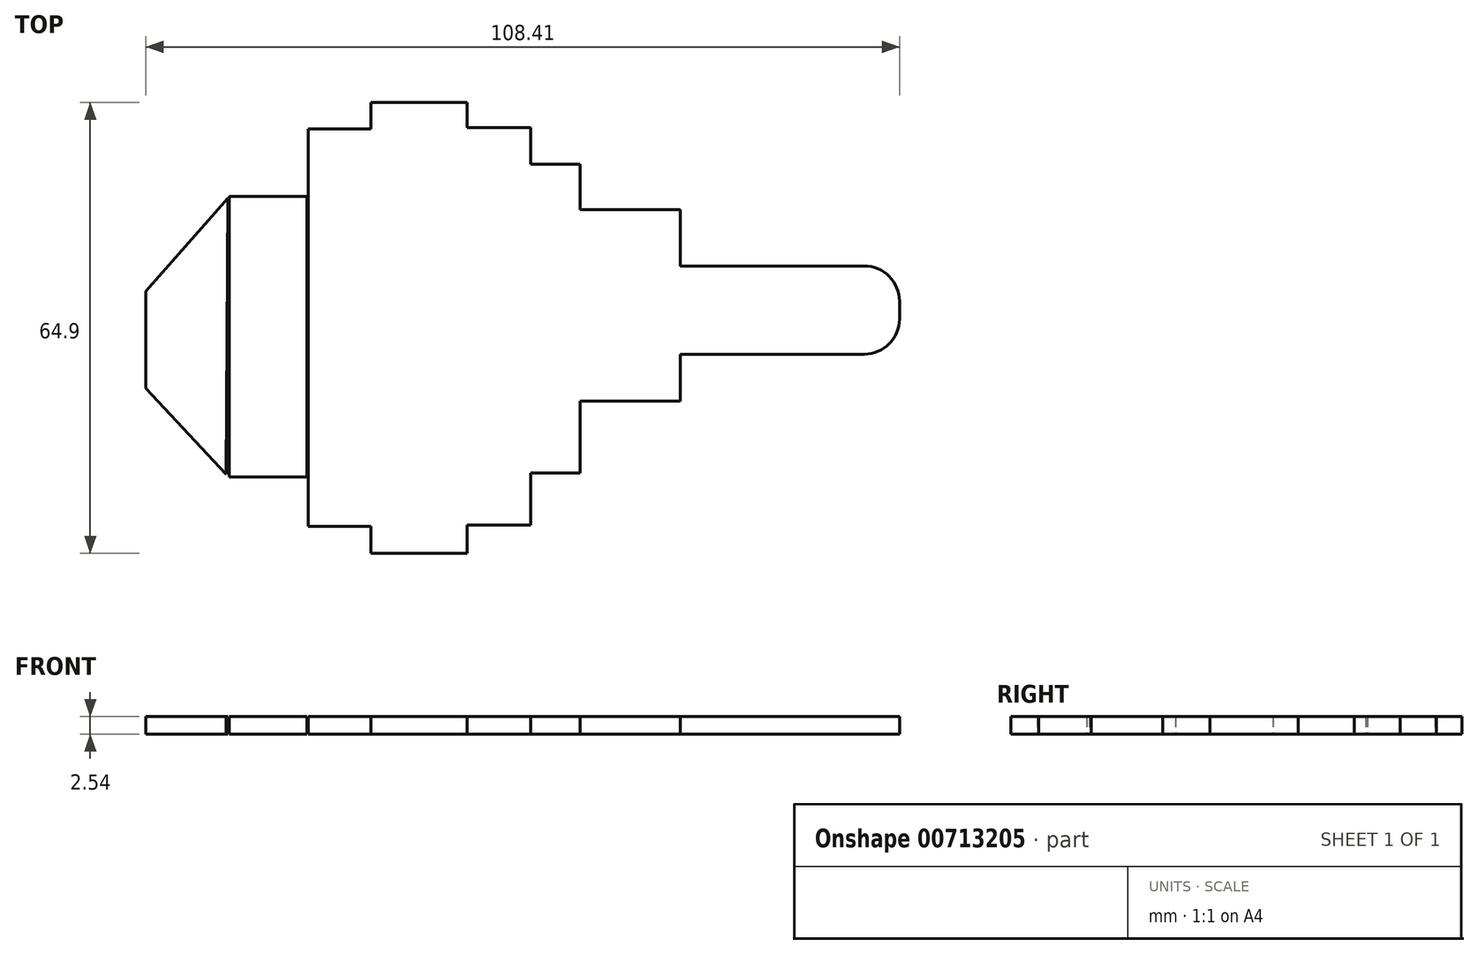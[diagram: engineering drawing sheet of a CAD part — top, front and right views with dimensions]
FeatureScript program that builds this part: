
annotation { "Feature Type Name" : "Feature", "Feature Type Description" : "" }
export const myFeature = defineFeature(function(context is Context, id is Id, definition is map)
    precondition{}
    {
        {
            var Q0;
            Q0=qCreatedBy(makeId("Top.planeOp"),FACE);
            var sketch = newSketch(context, id + "F0", { "sketchPlane" : qUnion([Q0])});
            skLineSegment(sketch, "E0.bottom", {"start": v(44.31, 7.48) * mm, "end": v(70.98, 7.48) * mm});
            skLineSegment(sketch, "E0.top", {"start": v(44.31, -5.22) * mm, "end": v(70.98, -5.22) * mm});
            skLineSegment(sketch, "E0.left", {"start": v(44.31, 7.48) * mm, "end": v(44.31, -5.22) * mm});
            skLineSegment(sketch, "E0.right", {"start": v(76.06, 2.4) * mm, "end": v(76.06, -0.14) * mm});
            skPoint(sketch, "E1.visualSharp", {"position": v(76.06, 7.48) * mm});
            skArc(sketch, "E1.filletArc", {"start": v(76.06, 2.4) * mm, "mid": v(74.58, 6) * mm, "end": v(70.98, 7.48) * mm});
            skPoint(sketch, "E2.visualSharp", {"position": v(76.06, -5.22) * mm});
            skArc(sketch, "E2.filletArc", {"start": v(70.98, -5.22) * mm, "mid": v(74.58, -3.73) * mm, "end": v(76.06, -0.14) * mm});
            skSolve(sketch);
        }
        {
            var Q0;
            Q0 = qSketchRegion(id + "F0", true);
            extrude(context, id + "F1", {"entities" : qUnion([Q0]), "depth" : 2.54 * mm, "offsetDistance" : 25.4 * mm});
        }
        {
            var Q0;
            Q0=qCreatedBy(makeId("Top.planeOp"),FACE);
            var sketch = newSketch(context, id + "F2", { "sketchPlane" : qUnion([Q0])});
            skLineSegment(sketch, "E3.bottom", {"start": v(44.52, -11.97) * mm, "end": v(29.92, -11.97) * mm});
            skLineSegment(sketch, "E3.top", {"start": v(44.52, 15.6) * mm, "end": v(29.92, 15.6) * mm});
            skLineSegment(sketch, "E3.left", {"start": v(44.52, -11.97) * mm, "end": v(44.52, 15.6) * mm});
            skLineSegment(sketch, "E3.right", {"start": v(29.92, -11.97) * mm, "end": v(29.92, 15.6) * mm});
            skPoint(sketch, "E3.middle", {"position": v(37.22, 1.81) * mm});
            skSolve(sketch);
        }
        {
            var Q0;
            Q0=makeQuery(id+"F2.imprint","IMPRINT",FACE,{"disambiguationData":[TD([[makeQuery(id+"F2.imprint","IMPRINT",EDGE,{"derivedFrom":sQuery(id+"F2.wireOp",EDGE,"E3.bottom")}),-1.0]])]});
            extrude(context, id + "F3", {"entities" : qUnion([Q0]), "operationType" : NewBodyOperationType.ADD, "depth" : 2.54 * mm, "offsetDistance" : 25.4 * mm});
        }
        {
            var Q0;
            Q0=qCreatedBy(makeId("Top.planeOp"),FACE);
            var sketch = newSketch(context, id + "F4", { "sketchPlane" : qUnion([Q0])});
            skLineSegment(sketch, "E4.bottom", {"start": v(30.12, 22.14) * mm, "end": v(22.61, 22.14) * mm});
            skLineSegment(sketch, "E4.top", {"start": v(30.12, -22.3) * mm, "end": v(22.61, -22.3) * mm});
            skLineSegment(sketch, "E4.left", {"start": v(30.12, 22.14) * mm, "end": v(30.12, -22.3) * mm});
            skLineSegment(sketch, "E4.right", {"start": v(22.61, 22.14) * mm, "end": v(22.61, -22.3) * mm});
            skSolve(sketch);
        }
        {
            var Q0;
            Q0 = qSketchRegion(id + "F4", true);
            extrude(context, id + "F5", {"entities" : qUnion([Q0]), "operationType" : NewBodyOperationType.ADD, "depth" : 2.54 * mm, "offsetDistance" : 25.4 * mm});
        }
        {
            var Q0;
            Q0=qCreatedBy(makeId("Top.planeOp"),FACE);
            var sketch = newSketch(context, id + "F6", { "sketchPlane" : qUnion([Q0])});
            skLineSegment(sketch, "E5.bottom", {"start": v(23.02, 27.38) * mm, "end": v(13.49, 27.38) * mm});
            skLineSegment(sketch, "E5.top", {"start": v(23.02, -29.81) * mm, "end": v(13.49, -29.81) * mm});
            skLineSegment(sketch, "E5.left", {"start": v(23.02, 27.38) * mm, "end": v(23.02, -29.81) * mm});
            skLineSegment(sketch, "E5.right", {"start": v(13.49, 27.38) * mm, "end": v(13.49, -29.81) * mm});
            skSolve(sketch);
        }
        {
            var Q0;
            Q0 = qSketchRegion(id + "F6", true);
            extrude(context, id + "F7", {"entities" : qUnion([Q0]), "operationType" : NewBodyOperationType.ADD, "depth" : 2.54 * mm, "offsetDistance" : 25.4 * mm});
        }
        {
            var Q0;
            Q0=qCreatedBy(makeId("Top.planeOp"),FACE);
            var sketch = newSketch(context, id + "F8", { "sketchPlane" : qUnion([Q0])});
            skLineSegment(sketch, "E6.bottom", {"start": v(13.84, 31.03) * mm, "end": v(0, 31.03) * mm});
            skLineSegment(sketch, "E6.top", {"start": v(13.84, -33.87) * mm, "end": v(0, -33.87) * mm});
            skLineSegment(sketch, "E6.left", {"start": v(13.84, 31.03) * mm, "end": v(13.84, -33.87) * mm});
            skLineSegment(sketch, "E6.right", {"start": v(0, 31.03) * mm, "end": v(0, -33.87) * mm});
            skSolve(sketch);
        }
        {
            var Q0;
            Q0 = qSketchRegion(id + "F8", true);
            extrude(context, id + "F9", {"entities" : qUnion([Q0]), "operationType" : NewBodyOperationType.ADD, "depth" : 2.54 * mm, "offsetDistance" : 25.4 * mm});
        }
        {
            var Q0;
            Q0=qCreatedBy(makeId("Top.planeOp"),FACE);
            var sketch = newSketch(context, id + "F10", { "sketchPlane" : qUnion([Q0])});
            skLineSegment(sketch, "E7.bottom", {"start": v(0.54, 27.18) * mm, "end": v(-8.99, 27.18) * mm});
            skLineSegment(sketch, "E7.top", {"start": v(0.54, -30.01) * mm, "end": v(-8.99, -30.01) * mm});
            skLineSegment(sketch, "E7.left", {"start": v(0.54, 27.18) * mm, "end": v(0.54, -30.01) * mm});
            skLineSegment(sketch, "E7.right", {"start": v(-8.99, 27.18) * mm, "end": v(-8.99, -30.01) * mm});
            skSolve(sketch);
        }
        {
            var Q0;
            Q0=makeQuery(id+"F10.imprint","IMPRINT",FACE,{"disambiguationData":[TD([[makeQuery(id+"F10.imprint","IMPRINT",EDGE,{"derivedFrom":sQuery(id+"F10.wireOp",EDGE,"E7.bottom")}),1.0]])]});
            extrude(context, id + "F11", {"entities" : qUnion([Q0]), "operationType" : NewBodyOperationType.ADD, "depth" : 2.54 * mm, "offsetDistance" : 25.4 * mm});
        }
        {
            var Q0;
            Q0=qCreatedBy(makeId("Top.planeOp"),FACE);
            var sketch = newSketch(context, id + "F12", { "sketchPlane" : qUnion([Q0])});
            skLineSegment(sketch, "E8.bottom", {"start": v(-9.2, 17.47) * mm, "end": v(-20.38, 17.47) * mm});
            skLineSegment(sketch, "E8.top", {"start": v(-9.2, -22.92) * mm, "end": v(-20.38, -22.92) * mm});
            skLineSegment(sketch, "E8.left", {"start": v(-9.2, 17.47) * mm, "end": v(-9.2, -22.92) * mm});
            skLineSegment(sketch, "E8.right", {"start": v(-20.38, 17.47) * mm, "end": v(-20.38, -22.92) * mm});
            skSolve(sketch);
        }
        {
            var Q0;
            Q0 = qSketchRegion(id + "F12", true);
            extrude(context, id + "F13", {"entities" : qUnion([Q0]), "depth" : 2.54 * mm, "offsetDistance" : 25.4 * mm});
        }
        {
            var Q0;
            Q0=qCreatedBy(makeId("Top.planeOp"),FACE);
            var sketch = newSketch(context, id + "F14", { "sketchPlane" : qUnion([Q0])});
            skLineSegment(sketch, "E9", {"start": v(-20.59, 17.24) * mm, "end": v(-32.35, 3.85) * mm});
            skLineSegment(sketch, "E10", {"start": v(-32.35, 3.85) * mm, "end": v(-32.35, -10.14) * mm});
            skLineSegment(sketch, "E11", {"start": v(-32.35, -10.14) * mm, "end": v(-20.79, -22.51) * mm});
            skLineSegment(sketch, "E12", {"start": v(-20.79, -22.51) * mm, "end": v(-20.59, 17.24) * mm});
            skSolve(sketch);
        }
        {
            var Q0;
            Q0=makeQuery(id+"F14.imprint","IMPRINT",FACE,{"disambiguationData":[TD([[makeQuery(id+"F14.imprint","IMPRINT",EDGE,{"derivedFrom":sQuery(id+"F14.wireOp",EDGE,"E9")}),1.0]])]});
            extrude(context, id + "F15", {"entities" : qUnion([Q0]), "depth" : 2.54 * mm, "offsetDistance" : 25.4 * mm});
        }
    });
